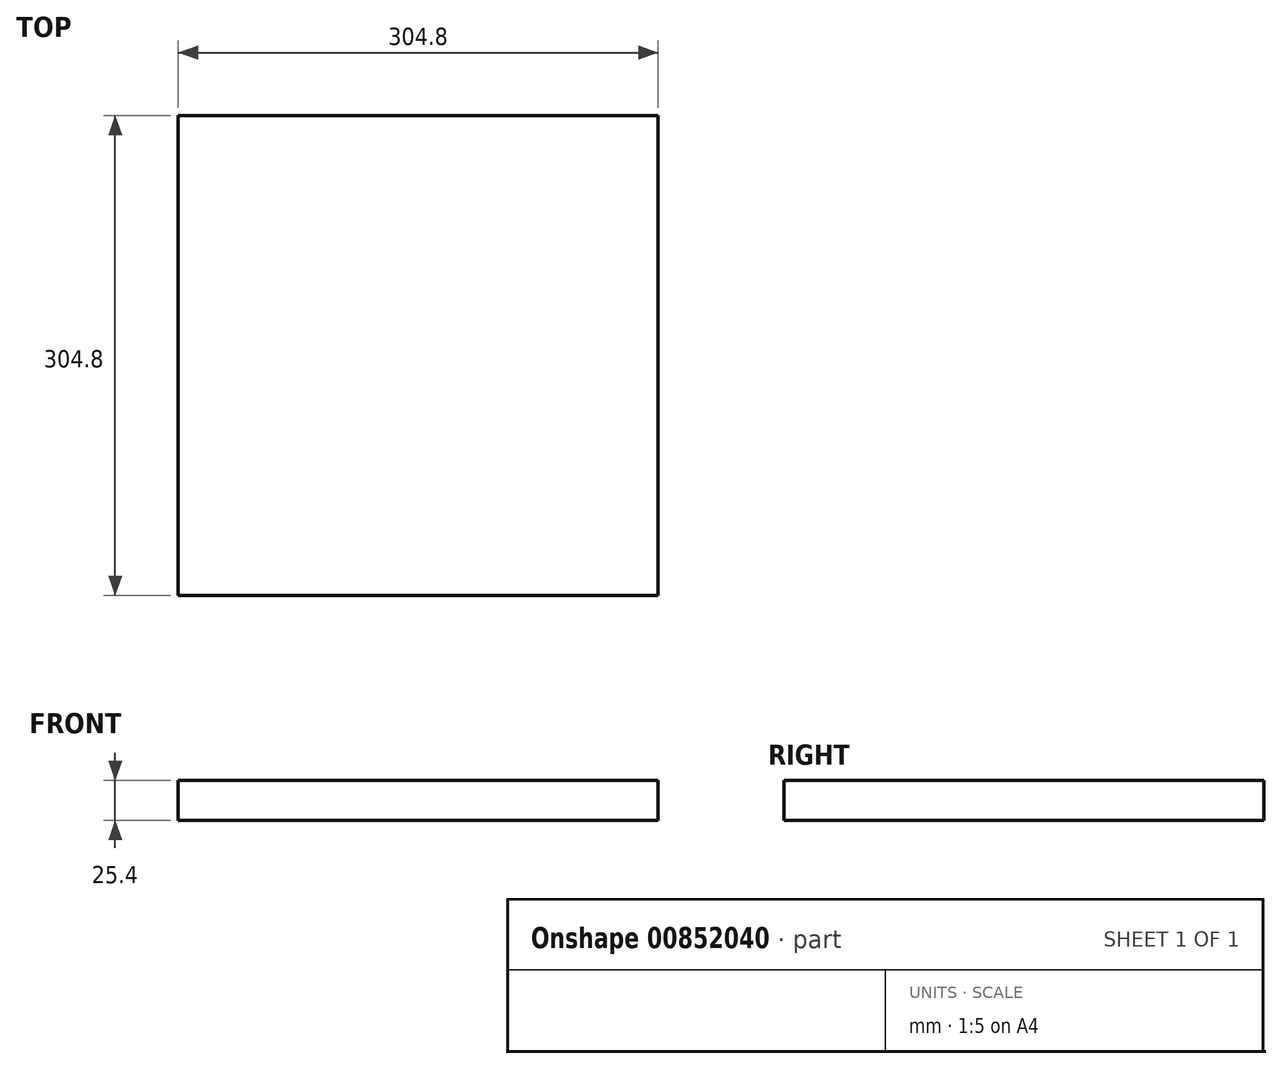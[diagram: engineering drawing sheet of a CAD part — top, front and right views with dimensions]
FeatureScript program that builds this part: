
annotation { "Feature Type Name" : "Feature", "Feature Type Description" : "" }
export const myFeature = defineFeature(function(context is Context, id is Id, definition is map)
    precondition{}
    {
        {
            var Q0;
            Q0=qCreatedBy(makeId("Top.planeOp"),FACE);
            var sketch = newSketch(context, id + "F0", { "sketchPlane" : qUnion([Q0])});
            skLineSegment(sketch, "E0.bottom", {"start": v(-152.4, 152.4) * mm, "end": v(152.4, 152.4) * mm});
            skLineSegment(sketch, "E0.top", {"start": v(-152.4, -152.4) * mm, "end": v(152.4, -152.4) * mm});
            skLineSegment(sketch, "E0.left", {"start": v(-152.4, 152.4) * mm, "end": v(-152.4, -152.4) * mm});
            skLineSegment(sketch, "E0.right", {"start": v(152.4, 152.4) * mm, "end": v(152.4, -152.4) * mm});
            skPoint(sketch, "E0.middle", {"position": v(0, 0) * mm});
            skSolve(sketch);
        }
        {
            var Q0;
            Q0 = qSketchRegion(id + "F0", true);
            extrude(context, id + "F1", {"entities" : qUnion([Q0]), "depth" : 25.4 * mm, "offsetDistance" : 25.4 * mm});
        }
    });
